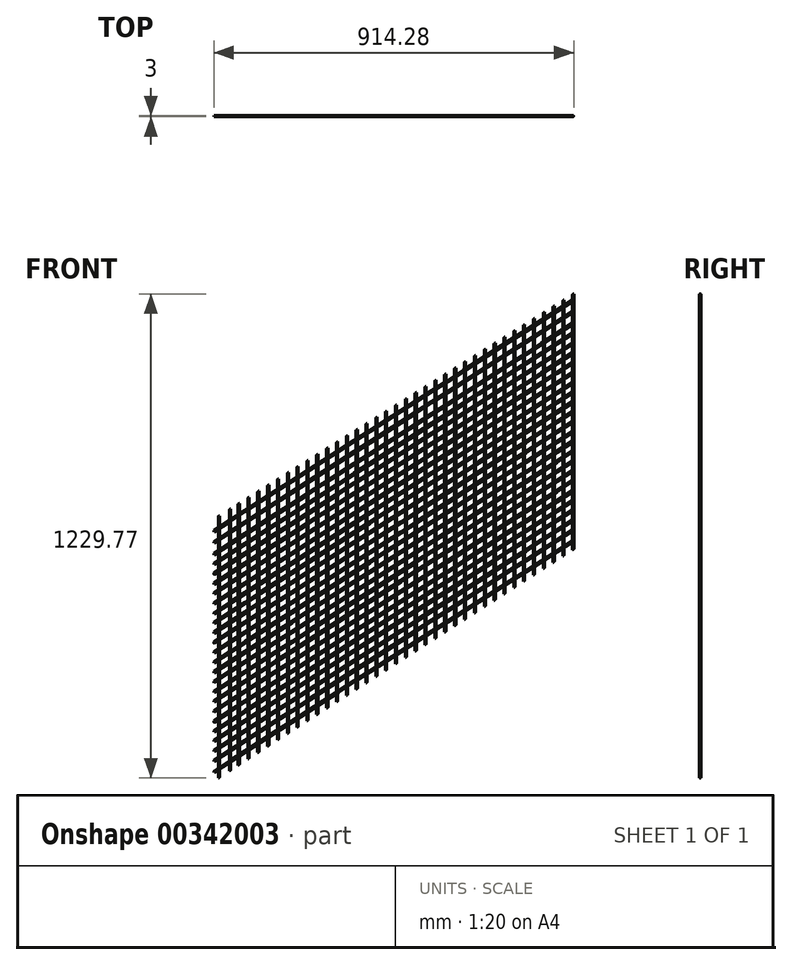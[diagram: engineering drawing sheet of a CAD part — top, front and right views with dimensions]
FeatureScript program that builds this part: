
annotation { "Feature Type Name" : "Feature", "Feature Type Description" : "" }
export const myFeature = defineFeature(function(context is Context, id is Id, definition is map)
    precondition{}
    {
        {
            var Q0;
            Q0=qCreatedBy(makeId("Front.planeOp"),FACE);
            var sketch = newSketch(context, id + "F0", { "sketchPlane" : qUnion([Q0])});
            skLineSegment(sketch, "E0", {"start": v(35, 122.75) * mm, "end": v(35, 802.75) * mm});
            skLineSegment(sketch, "E1", {"start": v(965, 727.25) * mm, "end": v(965, 1407.25) * mm});
            skLineSegment(sketch, "E2", {"start": v(965, 1407.25) * mm, "end": v(35, 802.75) * mm});
            skLineSegment(sketch, "E3", {"start": v(965, 727.25) * mm, "end": v(35, 122.75) * mm});
            skLineSegment(sketch, "E4", {"start": v(85, 214.1) * mm, "end": v(85, 775.62) * mm});
            skLineSegment(sketch, "E5", {"start": v(85, 775.62) * mm, "end": v(915, 1315.12) * mm});
            skLineSegment(sketch, "E6", {"start": v(915, 1315.12) * mm, "end": v(915, 756.37) * mm});
            skLineSegment(sketch, "E7", {"start": v(85, 214.1) * mm, "end": v(915, 756.37) * mm});
            skSolve(sketch);
        }
        {
            var Q0;
            Q0=qCreatedBy(makeId("Top.planeOp"),FACE);
            var sketch = newSketch(context, id + "F1", { "sketchPlane" : qUnion([Q0])});
            skCircle(sketch, "E8", {"center": v(34.23, 0) * mm, "radius": 1.5 * mm});
            skCircle(sketch, "E9", {"center": v(57.2, 0) * mm, "radius": 1.5 * mm});
            skCircle(sketch, "E10", {"center": v(85.02, 0) * mm, "radius": 1.5 * mm});
            skCircle(sketch, "E11", {"center": v(107.46, 0) * mm, "radius": 1.5 * mm});
            skCircle(sketch, "E12", {"center": v(132.15, 0) * mm, "radius": 1.5 * mm});
            skCircle(sketch, "E13", {"center": v(156.85, 0) * mm, "radius": 1.5 * mm});
            skCircle(sketch, "E14", {"center": v(182.21, 0) * mm, "radius": 1.5 * mm});
            skCircle(sketch, "E15", {"center": v(207.13, 0) * mm, "radius": 1.5 * mm});
            skCircle(sketch, "E16", {"center": v(232.27, 0) * mm, "radius": 1.5 * mm});
            skCircle(sketch, "E17", {"center": v(256.73, 0) * mm, "radius": 1.5 * mm});
            skCircle(sketch, "E18", {"center": v(281.65, 0) * mm, "radius": 1.5 * mm});
            skCircle(sketch, "E19", {"center": v(307.01, 0) * mm, "radius": 1.5 * mm});
            skCircle(sketch, "E20", {"center": v(332.38, 0) * mm, "radius": 1.5 * mm});
            skCircle(sketch, "E21", {"center": v(357.3, 0) * mm, "radius": 1.5 * mm});
            skCircle(sketch, "E22", {"center": v(381.98, 0) * mm, "radius": 1.5 * mm});
            skCircle(sketch, "E23", {"center": v(407.04, 0) * mm, "radius": 1.5 * mm});
            skCircle(sketch, "E24", {"center": v(432.12, 0) * mm, "radius": 1.5 * mm});
            skCircle(sketch, "E25", {"center": v(457.52, 0) * mm, "radius": 1.5 * mm});
            skCircle(sketch, "E26", {"center": v(481.64, 0) * mm, "radius": 1.5 * mm});
            skCircle(sketch, "E27", {"center": v(507.04, 0) * mm, "radius": 1.5 * mm});
            skCircle(sketch, "E28", {"center": v(532.43, 0) * mm, "radius": 1.5 * mm});
            skCircle(sketch, "E29", {"center": v(557.2, 0) * mm, "radius": 1.5 * mm});
            skCircle(sketch, "E30", {"center": v(581.95, 0) * mm, "radius": 1.5 * mm});
            skCircle(sketch, "E31", {"center": v(607.03, 0) * mm, "radius": 1.5 * mm});
            skCircle(sketch, "E32", {"center": v(632.11, 0) * mm, "radius": 1.5 * mm});
            skCircle(sketch, "E33", {"center": v(657.19, 0) * mm, "radius": 1.5 * mm});
            skCircle(sketch, "E34", {"center": v(682.27, 0) * mm, "radius": 1.5 * mm});
            skCircle(sketch, "E35", {"center": v(707.66, 0) * mm, "radius": 1.5 * mm});
            skCircle(sketch, "E36", {"center": v(732.74, 0) * mm, "radius": 1.5 * mm});
            skCircle(sketch, "E37", {"center": v(757.5, 0) * mm, "radius": 1.5 * mm});
            skCircle(sketch, "E38", {"center": v(782.26, 0) * mm, "radius": 1.5 * mm});
            skCircle(sketch, "E39", {"center": v(807.97, 0) * mm, "radius": 1.5 * mm});
            skCircle(sketch, "E40", {"center": v(832.15, 0) * mm, "radius": 1.5 * mm});
            skCircle(sketch, "E41", {"center": v(857.1, 0) * mm, "radius": 1.5 * mm});
            skCircle(sketch, "E42", {"center": v(882.46, 0) * mm, "radius": 1.5 * mm});
            skCircle(sketch, "E43", {"center": v(907.29, 0) * mm, "radius": 1.5 * mm});
            skCircle(sketch, "E44", {"center": v(931.98, 0) * mm, "radius": 1.5 * mm});
            skCircle(sketch, "E45", {"center": v(956.8, 0) * mm, "radius": 1.5 * mm});
            skSolve(sketch);
        }
        {
            var Q0;
            Q0 = qSketchRegion(id + "F1", true);
            extrude(context, id + "F2", {"entities" : qUnion([Q0]), "depth" : 2000 * mm});
        }
        {
            var Q0;
            Q0=qCreatedBy(makeId("Front.planeOp"),FACE);
            var sketch = newSketch(context, id + "F3", { "sketchPlane" : qUnion([Q0])});
            skLineSegment(sketch, "E46", {"start": v(0, 145.74) * mm, "end": v(957.48, 760.91) * mm});
            skLineSegment(sketch, "E47", {"start": v(0, 174.82) * mm, "end": v(958.44, 790.6) * mm});
            skLineSegment(sketch, "E48", {"start": v(0, 199.42) * mm, "end": v(959.72, 820.2) * mm});
            skLineSegment(sketch, "E49", {"start": v(0, 225.15) * mm, "end": v(958.7, 845.26) * mm});
            skLineSegment(sketch, "E50", {"start": v(0, 249.76) * mm, "end": v(958.6, 870.52) * mm});
            skLineSegment(sketch, "E51", {"start": v(0, 272.13) * mm, "end": v(957.48, 890.66) * mm});
            skLineSegment(sketch, "E52", {"start": v(0, 300.09) * mm, "end": v(957.43, 918.59) * mm});
            skLineSegment(sketch, "E53", {"start": v(0, 324.7) * mm, "end": v(958.04, 943.59) * mm});
            skLineSegment(sketch, "E54", {"start": v(0, 348.18) * mm, "end": v(956.46, 966.06) * mm});
            skLineSegment(sketch, "E55", {"start": v(0, 372.8) * mm, "end": v(956.46, 990.66) * mm});
            skLineSegment(sketch, "E56", {"start": v(0, 399.88) * mm, "end": v(956.81, 1018.77) * mm});
            skLineSegment(sketch, "E57", {"start": v(0, 422.45) * mm, "end": v(959.3, 1048.85) * mm});
            skLineSegment(sketch, "E58", {"start": v(0, 449.73) * mm, "end": v(955.58, 1073.7) * mm});
            skLineSegment(sketch, "E59", {"start": v(0, 474.5) * mm, "end": v(960.1, 1101.42) * mm});
            skLineSegment(sketch, "E60", {"start": v(0, 497.08) * mm, "end": v(961.2, 1124.72) * mm});
            skLineSegment(sketch, "E61", {"start": v(0, 523.42) * mm, "end": v(959.69, 1150.06) * mm});
            skLineSegment(sketch, "E62", {"start": v(0, 548.8) * mm, "end": v(957.35, 1176.15) * mm});
            skLineSegment(sketch, "E63", {"start": v(0, 575.15) * mm, "end": v(957.35, 1204.37) * mm});
            skLineSegment(sketch, "E64", {"start": v(0, 596.29) * mm, "end": v(958.72, 1224.52) * mm});
            skLineSegment(sketch, "E65", {"start": v(0, 622.89) * mm, "end": v(959.33, 1251.52) * mm});
            skLineSegment(sketch, "E66", {"start": v(0, 649.5) * mm, "end": v(956.89, 1276.53) * mm});
            skLineSegment(sketch, "E67", {"start": v(0, 674.76) * mm, "end": v(961.8, 1305.02) * mm});
            skLineSegment(sketch, "E68", {"start": v(0, 698.7) * mm, "end": v(955.91, 1325.1) * mm});
            skLineSegment(sketch, "E69", {"start": v(0, 723.8) * mm, "end": v(954.15, 1353.52) * mm});
            skLineSegment(sketch, "E70", {"start": v(0, 748.41) * mm, "end": v(960.86, 1371.42) * mm});
            skLineSegment(sketch, "E71", {"start": v(0, 774.14) * mm, "end": v(956.46, 1394.29) * mm});
            skSolve(sketch);
        }
        {
            var Q0;
            Q0=qCreatedBy(makeId("Right.planeOp"),FACE);
            var sketch = newSketch(context, id + "F4", { "sketchPlane" : qUnion([Q0])});
            skCircle(sketch, "E72", {"center": v(0, 145.54) * mm, "radius": 1.5 * mm});
            skCircle(sketch, "E73", {"center": v(0, 173.22) * mm, "radius": 1.5 * mm});
            skCircle(sketch, "E74", {"center": v(0, 198.23) * mm, "radius": 1.5 * mm});
            skCircle(sketch, "E75", {"center": v(0, 223.77) * mm, "radius": 1.5 * mm});
            skCircle(sketch, "E76", {"center": v(0, 248.38) * mm, "radius": 1.5 * mm});
            skCircle(sketch, "E77", {"center": v(0, 272.99) * mm, "radius": 1.5 * mm});
            skCircle(sketch, "E78", {"center": v(0, 298.43) * mm, "radius": 1.5 * mm});
            skCircle(sketch, "E79", {"center": v(0, 324.44) * mm, "radius": 1.5 * mm});
            skCircle(sketch, "E80", {"center": v(0, 348.48) * mm, "radius": 1.5 * mm});
            skCircle(sketch, "E81", {"center": v(0, 373.37) * mm, "radius": 1.5 * mm});
            skCircle(sketch, "E82", {"center": v(0, 398.45) * mm, "radius": 1.5 * mm});
            skCircle(sketch, "E83", {"center": v(0, 423.61) * mm, "radius": 1.5 * mm});
            skCircle(sketch, "E84", {"center": v(0, 448.43) * mm, "radius": 1.5 * mm});
            skCircle(sketch, "E85", {"center": v(0, 473.82) * mm, "radius": 1.5 * mm});
            skCircle(sketch, "E86", {"center": v(0, 498.98) * mm, "radius": 1.5 * mm});
            skCircle(sketch, "E87", {"center": v(0, 523.9) * mm, "radius": 1.5 * mm});
            skCircle(sketch, "E88", {"center": v(0, 548.12) * mm, "radius": 1.5 * mm});
            skCircle(sketch, "E89", {"center": v(0, 573.05) * mm, "radius": 1.5 * mm});
            skCircle(sketch, "E90", {"center": v(0, 598.2) * mm, "radius": 1.5 * mm});
            skCircle(sketch, "E91", {"center": v(0, 623.2) * mm, "radius": 1.5 * mm});
            skCircle(sketch, "E92", {"center": v(0, 648.52) * mm, "radius": 1.5 * mm});
            skCircle(sketch, "E93", {"center": v(0, 673.43) * mm, "radius": 1.5 * mm});
            skCircle(sketch, "E94", {"center": v(0, 698.15) * mm, "radius": 1.5 * mm});
            skCircle(sketch, "E95", {"center": v(0, 728.24) * mm, "radius": 1.5 * mm});
            skCircle(sketch, "E96", {"center": v(0, 756.84) * mm, "radius": 1.5 * mm});
            skSolve(sketch);
        }
        {
            var Q0;
            Q0=makeQuery(id+"F4.imprint","IMPRINT",FACE,{"disambiguationData":[TD([[makeQuery(id+"F4.imprint","IMPRINT",EDGE,{"derivedFrom":sQuery(id+"F4.wireOp",EDGE,"E72")}),1.0]])]});
            var Q1;
            Q1=makeQuery(id+"F4.imprint","IMPRINT",FACE,{"disambiguationData":[TD([[makeQuery(id+"F4.imprint","IMPRINT",EDGE,{"derivedFrom":sQuery(id+"F4.wireOp",EDGE,"E73")}),1.0]])]});
            var Q2;
            Q2=makeQuery(id+"F4.imprint","IMPRINT",FACE,{"disambiguationData":[TD([[makeQuery(id+"F4.imprint","IMPRINT",EDGE,{"derivedFrom":sQuery(id+"F4.wireOp",EDGE,"E74")}),1.0]])]});
            var Q3;
            Q3=makeQuery(id+"F4.imprint","IMPRINT",FACE,{"disambiguationData":[TD([[makeQuery(id+"F4.imprint","IMPRINT",EDGE,{"derivedFrom":sQuery(id+"F4.wireOp",EDGE,"E75")}),1.0]])]});
            var Q4;
            Q4=makeQuery(id+"F4.imprint","IMPRINT",FACE,{"disambiguationData":[TD([[makeQuery(id+"F4.imprint","IMPRINT",EDGE,{"derivedFrom":sQuery(id+"F4.wireOp",EDGE,"E76")}),1.0]])]});
            var Q5;
            Q5=makeQuery(id+"F4.imprint","IMPRINT",FACE,{"disambiguationData":[TD([[makeQuery(id+"F4.imprint","IMPRINT",EDGE,{"derivedFrom":sQuery(id+"F4.wireOp",EDGE,"E77")}),1.0]])]});
            var Q6;
            Q6=makeQuery(id+"F4.imprint","IMPRINT",FACE,{"disambiguationData":[TD([[makeQuery(id+"F4.imprint","IMPRINT",EDGE,{"derivedFrom":sQuery(id+"F4.wireOp",EDGE,"E78")}),1.0]])]});
            var Q7;
            Q7=makeQuery(id+"F4.imprint","IMPRINT",FACE,{"disambiguationData":[TD([[makeQuery(id+"F4.imprint","IMPRINT",EDGE,{"derivedFrom":sQuery(id+"F4.wireOp",EDGE,"E79")}),1.0]])]});
            var Q8;
            Q8=makeQuery(id+"F4.imprint","IMPRINT",FACE,{"disambiguationData":[TD([[makeQuery(id+"F4.imprint","IMPRINT",EDGE,{"derivedFrom":sQuery(id+"F4.wireOp",EDGE,"E80")}),1.0]])]});
            var Q9;
            Q9=makeQuery(id+"F4.imprint","IMPRINT",FACE,{"disambiguationData":[TD([[makeQuery(id+"F4.imprint","IMPRINT",EDGE,{"derivedFrom":sQuery(id+"F4.wireOp",EDGE,"E81")}),1.0]])]});
            var Q10;
            Q10=makeQuery(id+"F4.imprint","IMPRINT",FACE,{"disambiguationData":[TD([[makeQuery(id+"F4.imprint","IMPRINT",EDGE,{"derivedFrom":sQuery(id+"F4.wireOp",EDGE,"E82")}),1.0]])]});
            var Q11;
            Q11=makeQuery(id+"F4.imprint","IMPRINT",FACE,{"disambiguationData":[TD([[makeQuery(id+"F4.imprint","IMPRINT",EDGE,{"derivedFrom":sQuery(id+"F4.wireOp",EDGE,"E83")}),1.0]])]});
            var Q12;
            Q12=makeQuery(id+"F4.imprint","IMPRINT",FACE,{"disambiguationData":[TD([[makeQuery(id+"F4.imprint","IMPRINT",EDGE,{"derivedFrom":sQuery(id+"F4.wireOp",EDGE,"E84")}),1.0]])]});
            var Q13;
            Q13=makeQuery(id+"F4.imprint","IMPRINT",FACE,{"disambiguationData":[TD([[makeQuery(id+"F4.imprint","IMPRINT",EDGE,{"derivedFrom":sQuery(id+"F4.wireOp",EDGE,"E85")}),1.0]])]});
            var Q14;
            Q14=makeQuery(id+"F4.imprint","IMPRINT",FACE,{"disambiguationData":[TD([[makeQuery(id+"F4.imprint","IMPRINT",EDGE,{"derivedFrom":sQuery(id+"F4.wireOp",EDGE,"E86")}),1.0]])]});
            var Q15;
            Q15=makeQuery(id+"F4.imprint","IMPRINT",FACE,{"disambiguationData":[TD([[makeQuery(id+"F4.imprint","IMPRINT",EDGE,{"derivedFrom":sQuery(id+"F4.wireOp",EDGE,"E87")}),1.0]])]});
            var Q16;
            Q16=makeQuery(id+"F4.imprint","IMPRINT",FACE,{"disambiguationData":[TD([[makeQuery(id+"F4.imprint","IMPRINT",EDGE,{"derivedFrom":sQuery(id+"F4.wireOp",EDGE,"E88")}),1.0]])]});
            var Q17;
            Q17=makeQuery(id+"F4.imprint","IMPRINT",FACE,{"disambiguationData":[TD([[makeQuery(id+"F4.imprint","IMPRINT",EDGE,{"derivedFrom":sQuery(id+"F4.wireOp",EDGE,"E89")}),1.0]])]});
            var Q18;
            Q18=makeQuery(id+"F4.imprint","IMPRINT",FACE,{"disambiguationData":[TD([[makeQuery(id+"F4.imprint","IMPRINT",EDGE,{"derivedFrom":sQuery(id+"F4.wireOp",EDGE,"E90")}),1.0]])]});
            var Q19;
            Q19=makeQuery(id+"F4.imprint","IMPRINT",FACE,{"disambiguationData":[TD([[makeQuery(id+"F4.imprint","IMPRINT",EDGE,{"derivedFrom":sQuery(id+"F4.wireOp",EDGE,"E91")}),1.0]])]});
            var Q20;
            Q20=makeQuery(id+"F4.imprint","IMPRINT",FACE,{"disambiguationData":[TD([[makeQuery(id+"F4.imprint","IMPRINT",EDGE,{"derivedFrom":sQuery(id+"F4.wireOp",EDGE,"E92")}),1.0]])]});
            var Q21;
            Q21=makeQuery(id+"F4.imprint","IMPRINT",FACE,{"disambiguationData":[TD([[makeQuery(id+"F4.imprint","IMPRINT",EDGE,{"derivedFrom":sQuery(id+"F4.wireOp",EDGE,"E93")}),1.0]])]});
            var Q22;
            Q22=makeQuery(id+"F4.imprint","IMPRINT",FACE,{"disambiguationData":[TD([[makeQuery(id+"F4.imprint","IMPRINT",EDGE,{"derivedFrom":sQuery(id+"F4.wireOp",EDGE,"E94")}),1.0]])]});
            var Q23;
            Q23=makeQuery(id+"F4.imprint","IMPRINT",FACE,{"disambiguationData":[TD([[makeQuery(id+"F4.imprint","IMPRINT",EDGE,{"derivedFrom":sQuery(id+"F4.wireOp",EDGE,"E95")}),1.0]])]});
            var Q24;
            Q24=makeQuery(id+"F4.imprint","IMPRINT",FACE,{"disambiguationData":[TD([[makeQuery(id+"F4.imprint","IMPRINT",EDGE,{"derivedFrom":sQuery(id+"F4.wireOp",EDGE,"E96")}),1.0]])]});
            var Q25;
            Q25=sQuery(id+"F3.wireOp",EDGE,"E46");
            sweep(context, id + "F5", {"profiles" : qUnion([Q0, Q1, Q2, Q3, Q4, Q5, Q6, Q7, Q8, Q9, Q10, Q11, Q12, Q13, Q14, Q15, Q16, Q17, Q18, Q19, Q20, Q21, Q22, Q23, Q24]), "path" : qUnion([Q25])});
        }
        {
            var Q0;
            Q0=qCreatedBy(makeId("Front.planeOp"),FACE);
            var sketch = newSketch(context, id + "F6", { "sketchPlane" : qUnion([Q0])});
            skLineSegment(sketch, "E97", {"start": v(-13.34, 779.18) * mm, "end": v(1253.72, 1573.03) * mm});
            skLineSegment(sketch, "E98", {"start": v(1253.72, 1573.03) * mm, "end": v(1173.99, 2220.87) * mm});
            skLineSegment(sketch, "E99", {"start": v(1173.99, 2220.87) * mm, "end": v(-382.97, 2122.45) * mm});
            skLineSegment(sketch, "E100", {"start": v(-382.97, 2122.45) * mm, "end": v(-13.34, 779.18) * mm});
            skLineSegment(sketch, "E101", {"start": v(0, 122.28) * mm, "end": v(1642.18, 1180.37) * mm});
            skLineSegment(sketch, "E102", {"start": v(1642.18, 1180.37) * mm, "end": v(1406.7, -73.53) * mm});
            skLineSegment(sketch, "E103", {"start": v(1406.7, -73.53) * mm, "end": v(-129.76, -105.9) * mm});
            skLineSegment(sketch, "E104", {"start": v(-129.76, -105.9) * mm, "end": v(0, 122.28) * mm});
            skLineSegment(sketch, "E105", {"start": v(-23.62, 816.55) * mm, "end": v(44.03, 870.4) * mm});
            skLineSegment(sketch, "E106", {"start": v(44.03, 870.4) * mm, "end": v(44.03, 68.47) * mm});
            skLineSegment(sketch, "E107", {"start": v(44.03, 68.47) * mm, "end": v(-128.9, 68.47) * mm});
            skLineSegment(sketch, "E108", {"start": v(-128.9, 68.47) * mm, "end": v(-23.62, 816.55) * mm});
            skSolve(sketch);
        }
        {
            var Q0;
            Q0 = qSketchRegion(id + "F6", true);
            extrude(context, id + "F7", {"entities" : qUnion([Q0]), "operationType" : NewBodyOperationType.REMOVE, "endBound" : BoundingType.SYMMETRIC, "depth" : 1000 * mm});
        }
    });
